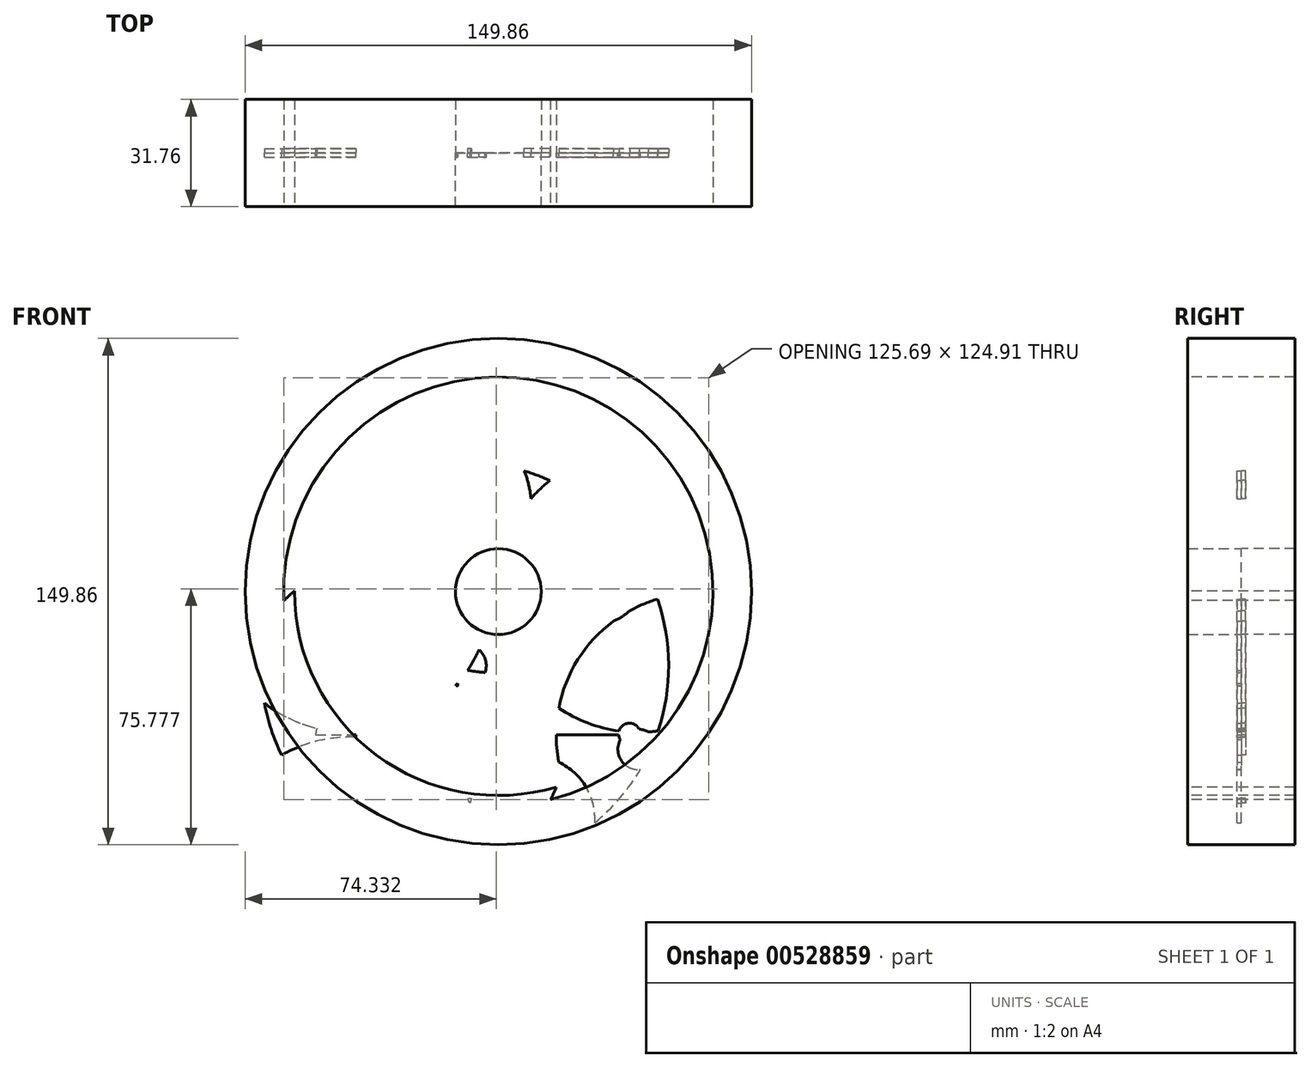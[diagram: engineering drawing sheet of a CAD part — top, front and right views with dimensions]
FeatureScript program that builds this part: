
annotation { "Feature Type Name" : "Feature", "Feature Type Description" : "" }
export const myFeature = defineFeature(function(context is Context, id is Id, definition is map)
    precondition{}
    {
        {
            var Q0;
            Q0=qCreatedBy(makeId("Front.planeOp"),FACE);
            var sketch = newSketch(context, id + "F0", { "sketchPlane" : qUnion([Q0])});
            skCircle(sketch, "E0", {"center": v(0, 0) * mm, "radius": 74.93 * mm});
            skCircle(sketch, "E1", {"center": v(0, 0) * mm, "radius": 6.35 * mm});
            skCircle(sketch, "E2", {"center": v(0, 0) * mm, "radius": 63.5 * mm});
            skArc(sketch, "E3", {"start": v(-36.2, -48.26) * mm, "mid": v(18.58, -15.1) * mm, "end": v(-4.56, 44.6) * mm});
            skLineSegment(sketch, "E4.1.0", {"start": v(-8.55, -59.72) * mm, "end": v(-8.55, -59.72) * mm});
            skArc(sketch, "E4.2.0", {"start": v(17.2, -57.82) * mm, "mid": v(18.9, -53.24) * mm, "end": v(20.16, -48.52) * mm});
            skArc(sketch, "E4.3.0", {"start": v(40.77, -44.46) * mm, "mid": v(0.5, 2.62) * mm, "end": v(-54.46, -25.94) * mm});
            skLineSegment(sketch, "E4.5.0", {"start": v(59.5, 9.88) * mm, "end": v(59.5, 9.88) * mm});
            skArc(sketch, "E4.6.0", {"start": v(60.31, -1.33) * mm, "mid": v(-39.17, 3.59) * mm, "end": v(60.27, -2.03) * mm});
            skArc(sketch, "E4.7.0", {"start": v(-58.45, 14.92) * mm, "mid": v(26.1, -26.27) * mm, "end": v(-14.54, 58.55) * mm});
            skPoint(sketch, "E4.center", {"position": v(-9, -18.6) * mm});
            skArc(sketch, "E5.trimOffspring", {"start": v(17.5, -57.73) * mm, "mid": v(14.1, -53.95) * mm, "end": v(9.74, -51.33) * mm});
            skPoint(sketch, "E6", {"position": v(0, 6.35) * mm});
            skCircle(sketch, "E7.0", {"center": v(0, 0) * mm, "radius": 12.7 * mm});
            skPoint(sketch, "E8.centerSnap0", {"position": v(3.49, -37.17) * mm});
            skArc(sketch, "E9.trimOffspring", {"start": v(20.16, -27.81) * mm, "mid": v(-12.2, 8.87) * mm, "end": v(-60.32, 0.19) * mm});
            skPoint(sketch, "E8.center.orphan", {"position": v(3.49, 34.19) * mm});
            skEllipticalArc(sketch, "E10", {});
            skEllipticalArc(sketch, "E11.1.0", {});
            skEllipticalArc(sketch, "E11.2.0", {});
            skEllipticalArc(sketch, "E11.3.0", {});
            skPoint(sketch, "E11.center", {"position": v(4.09, -0.57) * mm});
            skArc(sketch, "E12", {"start": v(20.16, -48.52) * mm, "mid": v(4.08, -0.55) * mm, "end": v(-45.67, 8.6) * mm});
            skEllipticalArc(sketch, "E13.trimOffspring", {});
            skEllipticalArc(sketch, "E14.trimOffspring", {});
            skEllipticalArc(sketch, "E15.trimOffspring", {});
            skArc(sketch, "E16.trimOffspring", {"start": v(60.1, -4.24) * mm, "mid": v(60.22, -2.78) * mm, "end": v(60.31, -1.33) * mm});
            skArc(sketch, "E17.trimOffspring", {"start": v(-4.56, 44.6) * mm, "mid": v(-18.29, 49.68) * mm, "end": v(-32.9, 50.56) * mm});
            skEllipticalArc(sketch, "E18.trimOffspring", {});
            skArc(sketch, "E19.trimOffspring", {"start": v(-43.7, 9.28) * mm, "mid": v(-53.57, -81.23) * mm, "end": v(20.16, -27.81) * mm});
            skArc(sketch, "E20.trimOffspring", {"start": v(-4.44, -51.76) * mm, "mid": v(-8.84, -54.83) * mm, "end": v(-12.08, -59.1) * mm});
            skArc(sketch, "E21", {"start": v(-8.55, -59.72) * mm, "mid": v(7.75, 3.93) * mm, "end": v(-53.25, 28.35) * mm});
            skArc(sketch, "E22", {"start": v(-60.32, 0.19) * mm, "mid": v(4.87, -60.13) * mm, "end": v(59.5, 9.88) * mm});
            skArc(sketch, "E23", {"start": v(-8.55, -59.72) * mm, "mid": v(27.8, -53.54) * mm, "end": v(53.77, -27.36) * mm});
            skArc(sketch, "E24.0", {"start": v(-46.95, 23.96) * mm, "mid": v(-48.7, 20.17) * mm, "end": v(-50.13, 16.26) * mm});
            skArc(sketch, "E25", {"start": v(53.77, -27.36) * mm, "mid": v(58.5, -14.71) * mm, "end": v(60.31, -1.33) * mm});
            skArc(sketch, "E26", {"start": v(60.31, -1.33) * mm, "mid": v(-39.01, 46.01) * mm, "end": v(-8.55, -59.72) * mm});
            skLineSegment(sketch, "E27", {"start": v(60.31, -1.33) * mm, "end": v(60.31, -1.33) * mm});
            skArc(sketch, "E28", {"start": v(59.5, 9.88) * mm, "mid": v(-16.6, 16.55) * mm, "end": v(-9.7, -59.54) * mm});
            skArc(sketch, "E29", {"start": v(59.5, 9.88) * mm, "mid": v(-60.17, -4.3) * mm, "end": v(60.31, -1.33) * mm});
            skArc(sketch, "E30", {"start": v(60.31, -1.33) * mm, "mid": v(0.76, 60.32) * mm, "end": v(-60.32, 0.19) * mm});
            skArc(sketch, "E31.0", {"start": v(47.4, -23.04) * mm, "mid": v(48.7, -20.14) * mm, "end": v(49.83, -17.17) * mm});
            skPoint(sketch, "E32", {"position": v(48.7, -20.14) * mm});
            skPoint(sketch, "E33", {"position": v(-48.7, 20.17) * mm});
            skCircle(sketch, "E34", {"center": v(-48.7, 20.17) * mm, "radius": 3.18 * mm});
            skCircle(sketch, "E35", {"center": v(48.7, -20.14) * mm, "radius": 3.18 * mm});
            skLineSegment(sketch, "E36", {"start": v(-36.66, -18.6) * mm, "end": v(18.66, -18.6) * mm});
            skCircle(sketch, "E37", {"center": v(-46.86, -18.6) * mm, "radius": 5.96 * mm});
            skCircle(sketch, "E38.1.0", {"center": v(18.6, -46.86) * mm, "radius": 5.96 * mm});
            skCircle(sketch, "E38.2.0", {"center": v(46.86, 18.6) * mm, "radius": 5.96 * mm});
            skCircle(sketch, "E38.3.0", {"center": v(-18.6, 46.86) * mm, "radius": 5.96 * mm});
            const initialGuessF0  = {"E10": [0, 0.024609249085187912, 0, -1, 0.01825924908518791, 0.010987894091327789, 0.6942682638491678, 2.7875886673787735], "E11.1.0": [-0.024609249085187912, 0, 1, 0, 0.01825924908518791, 0.010987894091327789, 3.4955966398008114, 5.588917043330419], "E11.2.0": [0, -0.024609249085187912, 0, 1, 0.01825924908518791, 0.010987894091327789, 0.6942682638491678, 2.7875886673787744], "E11.3.0": [0.024609249085187912, 0, -1, 0, 0.01825924908518791, 0.010987894091327789, 0.6942682638491678, 2.7875886673787735], "E13.trimOffspring": [-0.024609249085187912, 0, 1, 0, 0.01825924908518791, 0.010987894091327789, 0.6942682638491678, 2.7875886673787744], "E14.trimOffspring": [0, -0.024609249085187912, 0, 1, 0.01825924908518791, 0.010987894091327789, 3.4955966398008114, 5.588917043330419], "E15.trimOffspring": [0.024609249085187912, 0, -1, 0, 0.01825924908518791, 0.010987894091327789, 3.4955966398008123, 5.588917043330419], "E18.trimOffspring": [0, 0.024609249085187912, 0, -1, 0.01825924908518791, 0.010987894091327789, 3.4955966398008123, 5.588917043330419]};
            skSetInitialGuess(sketch, initialGuessF0);
            skSolve(sketch);
        }
        {
            var Q0;
            Q0=makeQuery(id+"F0.imprint","IMPRINT",FACE,{"disambiguationData":[TD([[makeQuery(id+"F0.imprint","IMPRINT",EDGE,{"derivedFrom":sQuery(id+"F0.wireOp",EDGE,"E2")}),1.0]])]});
            var Q1;
            Q1=makeQuery(id+"F0.imprint","IMPRINT",FACE,{"disambiguationData":[TD([[makeQuery(id+"F0.imprint","IMPRINT",EDGE,{"derivedFrom":sQuery(id+"F0.wireOp",EDGE,"E0")}),1.0]])]});
            extrude(context, id + "F1", {"entities" : qUnion([Q0, Q1]), "oppositeDirection" : true, "depth" : 15.88 * mm, "offsetDistance" : 25.4 * mm});
        }
        {
            var Q0;
            Q0=makeQuery(id+"F1.opExtrude","CAP_FACE",FACE,{"disambiguationData":[OSD([sQuery(id+"F0.wireOp",EDGE,"E0"),sQuery(id+"F0.wireOp",EDGE,"E23"),sQuery(id+"F0.wireOp",EDGE,"E29"),sQuery(id+"F0.wireOp",EDGE,"E30")])],"isStart":false});
            var Q1;
            Q1=makeQuery(id+"F1.opExtrude","CAP_FACE",FACE,{"disambiguationData":[OSD([sQuery(id+"F0.wireOp",EDGE,"E0"),sQuery(id+"F0.wireOp",EDGE,"E23"),sQuery(id+"F0.wireOp",EDGE,"E29"),sQuery(id+"F0.wireOp",EDGE,"E30")])],"isStart":true});
            extrude(context, id + "F2", {"entities" : qUnion([Q0, Q1]), "operationType" : NewBodyOperationType.ADD, "oppositeDirection" : true, "depth" : 15.88 * mm, "offsetDistance" : 25.4 * mm});
        }
        {
            var Q0;
            Q0=qCreatedBy(makeId("Front.planeOp"),FACE);
            var sketch = newSketch(context, id + "F3", { "sketchPlane" : qUnion([Q0])});
            skCircle(sketch, "E39", {"center": v(-9.92, -21.95) * mm, "radius": 74.93 * mm});
            skCircle(sketch, "E40", {"center": v(-9.92, -21.95) * mm, "radius": 6.35 * mm});
            skCircle(sketch, "E41", {"center": v(-9.92, -21.95) * mm, "radius": 63.5 * mm});
            skArc(sketch, "E42", {"start": v(-69.23, -32.98) * mm, "mid": v(-11.23, -26.13) * mm, "end": v(-16.58, 32.02) * mm});
            skLineSegment(sketch, "E43.1.0", {"start": v(-36.6, -76.06) * mm, "end": v(-36.6, -76.06) * mm});
            skArc(sketch, "E43.2.0", {"start": v(-2.02, -81.76) * mm, "mid": v(-12.24, -57.36) * mm, "end": v(-35.04, -43.96) * mm});
            skArc(sketch, "E43.3.0", {"start": v(25.81, -70.56) * mm, "mid": v(-5.7, -60.91) * mm, "end": v(-34.42, -77.07) * mm});
            skLineSegment(sketch, "E43.5.0", {"start": v(47.1, -2.23) * mm, "end": v(47.1, -2.23) * mm});
            skArc(sketch, "E43.6.0", {"start": v(15.23, 32.88) * mm, "mid": v(11.33, 29.34) * mm, "end": v(7.9, 25.33) * mm});
            skArc(sketch, "E43.7.0", {"start": v(-41.36, 29.53) * mm, "mid": v(-10.16, -23.05) * mm, "end": v(40.18, 11.66) * mm});
            skPoint(sketch, "E43.center", {"position": v(-1.2, -42.34) * mm});
            skArc(sketch, "E44.trimOffspring", {"start": v(28.6, -68.38) * mm, "mid": v(25.19, -56.62) * mm, "end": v(15.27, -49.45) * mm});
            skPoint(sketch, "E45", {"position": v(-9.92, -15.6) * mm});
            skCircle(sketch, "E46.0", {"center": v(-9.92, -21.95) * mm, "radius": 12.7 * mm});
            skPoint(sketch, "E47.centerSnap0", {"position": v(-18.07, -32.83) * mm});
            skPoint(sketch, "E48.center", {"position": v(-1.2, 0.2) * mm});
            skArc(sketch, "E49.trimOffspring", {"start": v(-52.44, -43.96) * mm, "mid": v(-58.46, -45.72) * mm, "end": v(-64.15, -48.36) * mm});
            skPoint(sketch, "E47.center.orphan", {"position": v(-18.07, 10.54) * mm});
            skEllipticalArc(sketch, "E50", {});
            skEllipticalArc(sketch, "E51.1.0", {});
            skEllipticalArc(sketch, "E51.2.0", {});
            skEllipticalArc(sketch, "E51.3.0", {});
            skPoint(sketch, "E51.center", {"position": v(-8.64, -11.15) * mm});
            skArc(sketch, "E52", {"start": v(-35.04, -43.96) * mm, "mid": v(-36.96, -43.6) * mm, "end": v(-38.9, -43.33) * mm});
            skEllipticalArc(sketch, "E53.trimOffspring", {});
            skEllipticalArc(sketch, "E54.trimOffspring", {});
            skEllipticalArc(sketch, "E55.trimOffspring", {});
            skArc(sketch, "E56.trimOffspring", {"start": v(11.15, -28.76) * mm, "mid": v(27.7, -39.35) * mm, "end": v(47.25, -41.22) * mm});
            skArc(sketch, "E57.trimOffspring", {"start": v(-16.58, 32.02) * mm, "mid": v(-19.93, 34.6) * mm, "end": v(-23.52, 36.82) * mm});
            skEllipticalArc(sketch, "E58.trimOffspring", {});
            skArc(sketch, "E59.trimOffspring", {"start": v(-38.9, -43.33) * mm, "mid": v(-45.7, -43.1) * mm, "end": v(-52.44, -43.96) * mm});
            skArc(sketch, "E60.trimOffspring", {"start": v(-3.58, -54.22) * mm, "mid": v(-9, -68.28) * mm, "end": v(-2.36, -81.8) * mm});
            skArc(sketch, "E61", {"start": v(-36.6, -76.06) * mm, "mid": v(-22.47, -26.93) * mm, "end": v(-66.42, -0.81) * mm});
            skArc(sketch, "E62", {"start": v(-64.15, -48.36) * mm, "mid": v(13.2, -77.67) * mm, "end": v(47.1, -2.23) * mm});
            skArc(sketch, "E63", {"start": v(-36.6, -76.06) * mm, "mid": v(9.12, -79.2) * mm, "end": v(43.85, -49.3) * mm});
            skArc(sketch, "E64.0", {"start": v(-56.86, 2) * mm, "mid": v(-58.6, -1.78) * mm, "end": v(-60.05, -5.7) * mm});
            skArc(sketch, "E65", {"start": v(43.85, -49.3) * mm, "mid": v(45.7, -45.32) * mm, "end": v(47.25, -41.22) * mm});
            skArc(sketch, "E66", {"start": v(47.25, -41.22) * mm, "mid": v(-33.06, 33.76) * mm, "end": v(-36.6, -76.06) * mm});
            skLineSegment(sketch, "E67", {"start": v(47.25, -41.22) * mm, "end": v(47.25, -41.22) * mm});
            skArc(sketch, "E68", {"start": v(47.1, -2.23) * mm, "mid": v(18.85, -30.47) * mm, "end": v(27.17, -69.53) * mm});
            skArc(sketch, "E69", {"start": v(47.1, -2.23) * mm, "mid": v(-70.24, -22.2) * mm, "end": v(47.25, -41.22) * mm});
            skArc(sketch, "E70", {"start": v(47.25, -41.22) * mm, "mid": v(-13.78, 38.25) * mm, "end": v(-64.15, -48.36) * mm});
            skArc(sketch, "E71.0", {"start": v(37.49, -44.99) * mm, "mid": v(38.79, -42.1) * mm, "end": v(39.91, -39.12) * mm});
            skPoint(sketch, "E72", {"position": v(38.79, -42.1) * mm});
            skPoint(sketch, "E73", {"position": v(-58.6, -1.78) * mm});
            skCircle(sketch, "E74", {"center": v(-58.6, -1.78) * mm, "radius": 3.18 * mm});
            skCircle(sketch, "E75", {"center": v(38.79, -42.1) * mm, "radius": 3.18 * mm});
            skLineSegment(sketch, "E76", {"start": v(-61.36, -42.34) * mm, "end": v(58.96, -42.34) * mm});
            skCircle(sketch, "E77", {"center": v(-48.06, -42.34) * mm, "radius": 5.96 * mm});
            skCircle(sketch, "E78.1.0", {"center": v(41.34, -46.67) * mm, "radius": 5.96 * mm});
            skCircle(sketch, "E78.2.0", {"center": v(45.66, 42.74) * mm, "radius": 5.96 * mm});
            skCircle(sketch, "E78.3.0", {"center": v(-43.74, 47.06) * mm, "radius": 5.96 * mm});
            const initialGuessF3  = {"E50": [-0.0012004772369377595, 0.024807692092965256, 0, -1, 0.01825924908518791, 0.010987894091327789, 0.6942682638491678, 2.7875886673787735], "E51.1.0": [-0.025809726322125668, 0.00019844300777734197, 1, 0, 0.01825924908518791, 0.010987894091327789, 3.4955966398008114, 5.588917043330419], "E51.2.0": [-0.0012004772369377551, -0.024410806077410568, 0, 1, 0.01825924908518791, 0.010987894091327789, 0.6942682638491678, 2.7875886673787744], "E51.3.0": [0.023408771848250156, 0.0001984430077773432, -1, 0, 0.01825924908518791, 0.010987894091327789, 0.6942682638491678, 2.7875886673787735], "E53.trimOffspring": [-0.025809726322125668, 0.00019844300777734197, 1, 0, 0.01825924908518791, 0.010987894091327789, 0.6942682638491678, 2.7875886673787744], "E54.trimOffspring": [-0.0012004772369377551, -0.024410806077410568, 0, 1, 0.01825924908518791, 0.010987894091327789, 3.4955966398008114, 5.588917043330419], "E55.trimOffspring": [0.023408771848250156, 0.0001984430077773432, -1, 0, 0.01825924908518791, 0.010987894091327789, 3.4955966398008123, 5.588917043330419], "E58.trimOffspring": [-0.0012004772369377595, 0.024807692092965256, 0, -1, 0.01825924908518791, 0.010987894091327789, 3.4955966398008123, 5.588917043330419]};
            skSetInitialGuess(sketch, initialGuessF3);
            skSolve(sketch);
        }
        {
            var Q0;
            Q0 = qSketchRegion(id + "F808i7j2Hfvb2gE_1", true);
            var Q1;
            {var subQ6=sQuery(id+"F3.wireOp",EDGE,"E43.2.0");Q1=makeQuery(id+"F3.imprint","IMPRINT",FACE,{"disambiguationData":[TD([[makeQuery(id+"F3.imprint","IMPRINT",EDGE,{"derivedFrom":subQ6}),-1.0]])]});}
            var Q2;
            {var subQ15=sQuery(id+"F3.wireOp",EDGE,"E49.trimOffspring");Q2=makeQuery(id+"F3.imprint","IMPRINT",FACE,{"disambiguationData":[TD([[makeQuery(id+"F3.imprint","IMPRINT",EDGE,{"derivedFrom":subQ15}),-1.0]])]});}
            var Q3;
            {var subQ8=sQuery(id+"F3.wireOp",EDGE,"E42");Q3=makeQuery(id+"F3.imprint","IMPRINT",FACE,{"disambiguationData":[TD([[makeQuery(id+"F3.imprint","IMPRINT",EDGE,{"derivedFrom":subQ8}),-1.0]])]});}
            var Q4;
            {var subQ5=sQuery(id+"F3.wireOp",EDGE,"E43.6.0");Q4=makeQuery(id+"F3.imprint","IMPRINT",FACE,{"disambiguationData":[TD([[makeQuery(id+"F3.imprint","IMPRINT",EDGE,{"derivedFrom":subQ5}),-1.0]])]});}
            var Q5;
            {var subQ1=sQuery(id+"F3.wireOp",EDGE,"E44.trimOffspring");Q5=makeQuery(id+"F3.imprint","IMPRINT",FACE,{"disambiguationData":[TD([[makeQuery(id+"F3.imprint","IMPRINT",EDGE,{"derivedFrom":subQ1}),-1.0]])]});}
            var Q6;
            {var subQ8=sQuery(id+"F3.wireOp",EDGE,"E51.3.0");Q6=makeQuery(id+"F3.imprint","IMPRINT",FACE,{"disambiguationData":[TD([[makeQuery(id+"F3.imprint","IMPRINT",EDGE,{"derivedFrom":subQ8}),-1.0]])]});}
            extrude(context, id + "F4", {"entities" : qUnion([Q0, Q1, Q2, Q3, Q4, Q5, Q6]), "depth" : 1.27 * mm, "offsetDistance" : 25.4 * mm});
        }
        {
            var Q0;
            Q0=makeQuery(id+"F4.opExtrude","CAP_FACE",FACE,{"disambiguationData":[OSD([sQuery(id+"F3.wireOp",EDGE,"E43.6.0"),sQuery(id+"F3.wireOp",EDGE,"E43.7.0"),sQuery(id+"F3.wireOp",EDGE,"E46.0"),sQuery(id+"F3.wireOp",EDGE,"E50"),sQuery(id+"F3.wireOp",EDGE,"E55.trimOffspring"),sQuery(id+"F3.wireOp",EDGE,"E57.trimOffspring"),sQuery(id+"F3.wireOp",EDGE,"E70"),sQuery(id+"F3.wireOp",EDGE,"E78.3.0")])],"isStart":true});
            var Q1;
            Q1=makeQuery(id+"F4.opExtrude","CAP_FACE",FACE,{"disambiguationData":[OSD([sQuery(id+"F3.wireOp",EDGE,"E42"),sQuery(id+"F3.wireOp",EDGE,"E46.0"),sQuery(id+"F3.wireOp",EDGE,"E49.trimOffspring"),sQuery(id+"F3.wireOp",EDGE,"E53.trimOffspring"),sQuery(id+"F3.wireOp",EDGE,"E58.trimOffspring"),sQuery(id+"F3.wireOp",EDGE,"E59.trimOffspring"),sQuery(id+"F3.wireOp",EDGE,"E61"),sQuery(id+"F3.wireOp",EDGE,"E70"),sQuery(id+"F3.wireOp",EDGE,"E74"),sQuery(id+"F3.wireOp",EDGE,"E77")])],"isStart":true});
            var Q2;
            Q2=makeQuery(id+"F4.opExtrude","CAP_FACE",FACE,{"disambiguationData":[OSD([sQuery(id+"F3.wireOp",EDGE,"E44.trimOffspring"),sQuery(id+"F3.wireOp",EDGE,"E46.0"),sQuery(id+"F3.wireOp",EDGE,"E51.3.0"),sQuery(id+"F3.wireOp",EDGE,"E54.trimOffspring"),sQuery(id+"F3.wireOp",EDGE,"E56.trimOffspring"),sQuery(id+"F3.wireOp",EDGE,"E63"),sQuery(id+"F3.wireOp",EDGE,"E68"),sQuery(id+"F3.wireOp",EDGE,"E69"),sQuery(id+"F3.wireOp",EDGE,"E75"),sQuery(id+"F3.wireOp",EDGE,"E78.2.0")])],"isStart":true});
            var Q3;
            Q3=makeQuery(id+"F4.opExtrude","CAP_FACE",FACE,{"disambiguationData":[OSD([sQuery(id+"F3.wireOp",EDGE,"E43.2.0"),sQuery(id+"F3.wireOp",EDGE,"E43.3.0"),sQuery(id+"F3.wireOp",EDGE,"E46.0"),sQuery(id+"F3.wireOp",EDGE,"E51.1.0"),sQuery(id+"F3.wireOp",EDGE,"E51.2.0"),sQuery(id+"F3.wireOp",EDGE,"E52"),sQuery(id+"F3.wireOp",EDGE,"E60.trimOffspring"),sQuery(id+"F3.wireOp",EDGE,"E63"),sQuery(id+"F3.wireOp",EDGE,"E78.1.0")])],"isStart":true});
            extrude(context, id + "F5", {"entities" : qUnion([Q0, Q1, Q2, Q3]), "depth" : 1.27 * mm, "offsetDistance" : 25.4 * mm});
        }
        {
            var Q0;
            Q0=qCreatedBy(makeId("Front.planeOp"),FACE);
            var sketch = newSketch(context, id + "F6", { "sketchPlane" : qUnion([Q0])});
            skCircle(sketch, "E79", {"center": v(0, 0) * mm, "radius": 12.7 * mm});
            skCircle(sketch, "E80", {"center": v(0, 0) * mm, "radius": 6.35 * mm});
            skSolve(sketch);
        }
        {
            var Q0;
            Q0=makeQuery(id+"F6.imprint","IMPRINT",FACE,{"disambiguationData":[TD([[makeQuery(id+"F6.imprint","IMPRINT",EDGE,{"derivedFrom":sQuery(id+"F6.wireOp",EDGE,"E79")}),1.0]])]});
            var Q1;
            Q1=makeQuery(id+"F6.imprint","IMPRINT",FACE,{"disambiguationData":[TD([[makeQuery(id+"F6.imprint","IMPRINT",EDGE,{"derivedFrom":sQuery(id+"F6.wireOp",EDGE,"E80")}),1.0]])]});
            extrude(context, id + "F7", {"entities" : qUnion([Q0, Q1]), "depth" : 15.88 * mm, "offsetDistance" : 25.4 * mm});
        }
        {
            var Q0;
            Q0=makeQuery(id+"F7.opExtrude","CAP_FACE",FACE,{"disambiguationData":[OSD([sQuery(id+"F6.wireOp",EDGE,"E79")])],"isStart":true});
            extrude(context, id + "F8", {"entities" : qUnion([Q0]), "depth" : 15.88 * mm, "offsetDistance" : 25.4 * mm});
        }
    });
